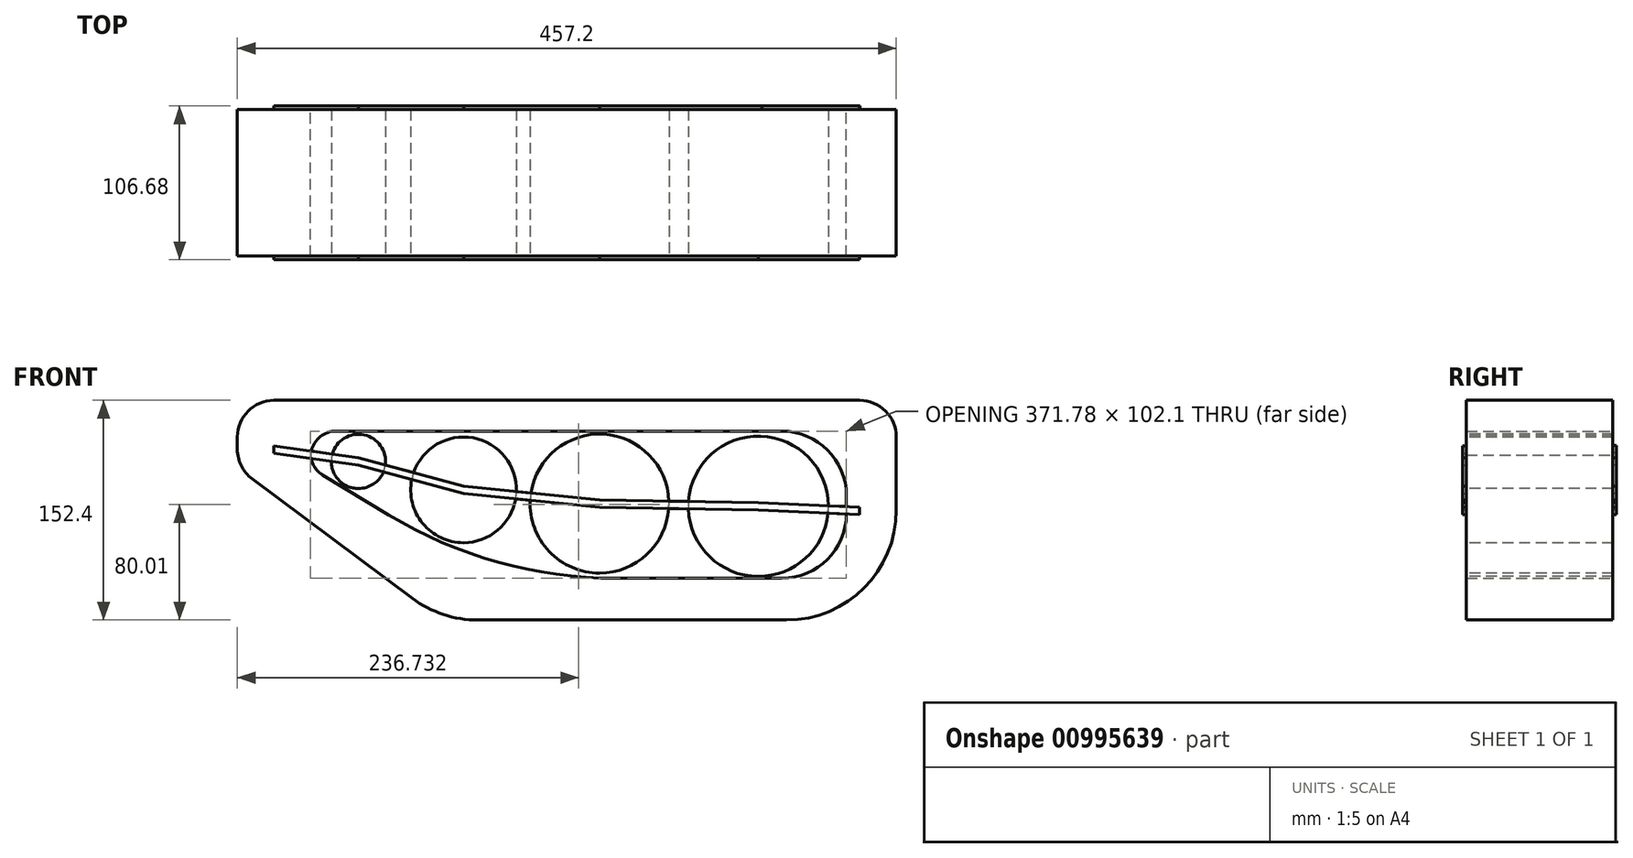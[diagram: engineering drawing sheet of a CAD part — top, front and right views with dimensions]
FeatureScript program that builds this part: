
annotation { "Feature Type Name" : "Feature", "Feature Type Description" : "" }
export const myFeature = defineFeature(function(context is Context, id is Id, definition is map)
    precondition{}
    {
        {
            var Q0;
            Q0=qCreatedBy(makeId("Front.planeOp"),FACE);
            var sketch = newSketch(context, id + "F0", { "sketchPlane" : qUnion([Q0])});
            skLineSegment(sketch, "E0.top", {"start": v(228.6, 76.2) * mm, "end": v(-228.6, 76.2) * mm});
            skLineSegment(sketch, "E0.left", {"start": v(228.6, -76.2) * mm, "end": v(228.6, 76.2) * mm});
            skPoint(sketch, "E0.middle", {"position": v(0, 0) * mm});
            skLineSegment(sketch, "E1", {"start": v(-228.6, 29.46) * mm, "end": v(-86.97, -76.2) * mm});
            skLineSegment(sketch, "E2", {"start": v(-177.8, 29.46) * mm, "end": v(-50.81, -47.24) * mm});
            skLineSegment(sketch, "E3", {"start": v(-50.81, -47.24) * mm, "end": v(194.02, -47.24) * mm});
            skLineSegment(sketch, "E4", {"start": v(-86.97, -76.2) * mm, "end": v(228.6, -76.2) * mm});
            skLineSegment(sketch, "E5", {"start": v(-228.6, 76.2) * mm, "end": v(-228.6, 29.46) * mm});
            skLineSegment(sketch, "E6", {"start": v(-177.8, 29.46) * mm, "end": v(-177.8, 54.86) * mm});
            skLineSegment(sketch, "E7", {"start": v(-177.8, 54.86) * mm, "end": v(194.02, 54.86) * mm});
            skLineSegment(sketch, "E8", {"start": v(194.02, 54.86) * mm, "end": v(194.02, -47.24) * mm});
            skSolve(sketch);
        }
        {
            var Q0;
            Q0=makeQuery(id+"F0.imprint","IMPRINT",FACE,{"disambiguationData":[TD([[makeQuery(id+"F0.imprint","IMPRINT",EDGE,{"derivedFrom":sQuery(id+"F0.wireOp",EDGE,"E0.top")}),1.0]])]});
            extrude(context, id + "F1", {"entities" : qUnion([Q0]), "depth" : 101.6 * mm, "offsetDistance" : 25.4 * mm});
        }
        {
            var Q0;
            Q0=makeQuery(id+"F1.opExtrude","SWEPT_EDGE",EDGE,{"disambiguationData":[OSD([sQuery(id+"F0.wireOp",EDGE,"E0.top"),sQuery(id+"F0.wireOp",EDGE,"E5")])]});
            var Q1;
            Q1=makeQuery(id+"F1.opExtrude","SWEPT_EDGE",EDGE,{"disambiguationData":[OSD([sQuery(id+"F0.wireOp",EDGE,"E1"),sQuery(id+"F0.wireOp",EDGE,"E5")])]});
            fillet(context, id + "F2", {"entities" : qUnion([Q0, Q1]), "radius" : 25.4 * mm, "tangentPropagation" : true, "allowEdgeOverflow" : false});
        }
        {
            var Q0;
            Q0=makeQuery(id+"F1.opExtrude","SWEPT_EDGE",EDGE,{"disambiguationData":[OSD([sQuery(id+"F0.wireOp",EDGE,"E1"),sQuery(id+"F0.wireOp",EDGE,"E4")])]});
            var Q1;
            Q1=makeQuery(id+"F1.opExtrude","SWEPT_EDGE",EDGE,{"disambiguationData":[OSD([sQuery(id+"F0.wireOp",EDGE,"E0.left"),sQuery(id+"F0.wireOp",EDGE,"E4")])]});
            fillet(context, id + "F3", {"entities" : qUnion([Q0, Q1]), "radius" : 76.2 * mm, "tangentPropagation" : true, "allowEdgeOverflow" : false});
        }
        {
            var Q0;
            Q0=makeQuery(id+"F1.opExtrude","SWEPT_EDGE",EDGE,{"disambiguationData":[OSD([sQuery(id+"F0.wireOp",EDGE,"E0.top"),sQuery(id+"F0.wireOp",EDGE,"E0.left")])]});
            fillet(context, id + "F4", {"entities" : qUnion([Q0]), "radius" : 25.4 * mm, "tangentPropagation" : true, "allowEdgeOverflow" : false});
        }
        {
            var Q0;
            Q0=makeQuery(id+"F1.opExtrude","SWEPT_EDGE",EDGE,{"disambiguationData":[OSD([sQuery(id+"F0.wireOp",EDGE,"E2"),sQuery(id+"F0.wireOp",EDGE,"E6")])]});
            var Q1;
            Q1=makeQuery(id+"F1.opExtrude","SWEPT_EDGE",EDGE,{"disambiguationData":[OSD([sQuery(id+"F0.wireOp",EDGE,"E6"),sQuery(id+"F0.wireOp",EDGE,"E7")])]});
            fillet(context, id + "F5", {"entities" : qUnion([Q0, Q1]), "radius" : 17.78 * mm, "tangentPropagation" : true, "allowEdgeOverflow" : false});
        }
        {
            var Q0;
            Q0=makeQuery(id+"F1.opExtrude","SWEPT_EDGE",EDGE,{"disambiguationData":[OSD([sQuery(id+"F0.wireOp",EDGE,"E3"),sQuery(id+"F0.wireOp",EDGE,"E8")])]});
            var Q1;
            Q1=makeQuery(id+"F1.opExtrude","SWEPT_EDGE",EDGE,{"disambiguationData":[OSD([sQuery(id+"F0.wireOp",EDGE,"E7"),sQuery(id+"F0.wireOp",EDGE,"E8")])]});
            fillet(context, id + "F6", {"entities" : qUnion([Q0, Q1]), "radius" : 44.76 * mm, "tangentPropagation" : true, "allowEdgeOverflow" : false});
        }
        {
            var Q0;
            Q0=makeQuery(id+"F1.opExtrude","SWEPT_EDGE",EDGE,{"disambiguationData":[OSD([sQuery(id+"F0.wireOp",EDGE,"E2"),sQuery(id+"F0.wireOp",EDGE,"E3")])]});
            fillet(context, id + "F7", {"entities" : qUnion([Q0]), "radius" : 304.8 * mm, "tangentPropagation" : true, "allowEdgeOverflow" : false});
        }
        {
            var Q0;
            Q0=makeQuery(id+"F1.opExtrude","CAP_FACE",FACE,{"disambiguationData":[OSD([sQuery(id+"F0.wireOp",EDGE,"E0.top"),sQuery(id+"F0.wireOp",EDGE,"E0.left"),sQuery(id+"F0.wireOp",EDGE,"E1"),sQuery(id+"F0.wireOp",EDGE,"E2"),sQuery(id+"F0.wireOp",EDGE,"E3"),sQuery(id+"F0.wireOp",EDGE,"E4"),sQuery(id+"F0.wireOp",EDGE,"E5"),sQuery(id+"F0.wireOp",EDGE,"E6"),sQuery(id+"F0.wireOp",EDGE,"E7"),sQuery(id+"F0.wireOp",EDGE,"E8")])],"isStart":false});
            var sketch = newSketch(context, id + "F8", { "sketchPlane" : qUnion([Q0])});
            skCircle(sketch, "E9", {"center": v(-144.6, 33.85) * mm, "radius": 18.83 * mm});
            skPoint(sketch, "E9.first.point", {"position": v(-138.02, 51.5) * mm});
            skPoint(sketch, "E9.second.point", {"position": v(-146.35, 15.1) * mm});
            skPoint(sketch, "E9.second.point.positionSnap0", {"position": v(-146.35, 10.46) * mm});
            skPoint(sketch, "E9.third.point", {"position": v(-127.18, 26.71) * mm});
            skCircle(sketch, "E10", {"center": v(-71.64, 14.1) * mm, "radius": 36.66 * mm});
            skPoint(sketch, "E10.first.point", {"position": v(-73.36, 50.72) * mm});
            skPoint(sketch, "E10.second.point", {"position": v(-65.62, -22.07) * mm});
            skPoint(sketch, "E10.third.point", {"position": v(-50.52, -15.87) * mm});
            skCircle(sketch, "E11", {"center": v(22.69, 4.6) * mm, "radius": 48.18 * mm});
            skPoint(sketch, "E11.first.point", {"position": v(6.39, 49.94) * mm});
            skPoint(sketch, "E11.second.point", {"position": v(41.23, -39.88) * mm});
            skPoint(sketch, "E11.third.point", {"position": v(61.75, -23.62) * mm});
            skCircle(sketch, "E12", {"center": v(132.93, 2.7) * mm, "radius": 48.63 * mm});
            skPoint(sketch, "E12.first.point", {"position": v(129.96, 51.24) * mm});
            skPoint(sketch, "E12.second.point", {"position": v(126.16, -45.46) * mm});
            skPoint(sketch, "E12.third.point", {"position": v(181.18, -3.34) * mm});
            skLineSegment(sketch, "E13", {"start": v(-203.2, 42.2) * mm, "end": v(-203.2, 44.74) * mm});
            skLineSegment(sketch, "E14", {"start": v(-203.2, 42.2) * mm, "end": v(-203.2, 39.66) * mm});
            skLineSegment(sketch, "E15", {"start": v(203.2, -0.41) * mm, "end": v(203.2, -2.95) * mm});
            skLineSegment(sketch, "E16", {"start": v(203.2, -0.41) * mm, "end": v(203.2, 2.13) * mm});
            skLineSegment(sketch, "E17", {"start": v(-203.2, 44.74) * mm, "end": v(-144.6, 36.39) * mm});
            skLineSegment(sketch, "E18", {"start": v(-144.6, 36.39) * mm, "end": v(-71.64, 16.64) * mm});
            skLineSegment(sketch, "E19", {"start": v(-71.64, 16.64) * mm, "end": v(22.69, 7.14) * mm});
            skLineSegment(sketch, "E20", {"start": v(22.69, 7.14) * mm, "end": v(132.93, 5.24) * mm});
            skLineSegment(sketch, "E21", {"start": v(132.93, 5.24) * mm, "end": v(203.2, 2.13) * mm});
            skLineSegment(sketch, "E22", {"start": v(203.2, -2.95) * mm, "end": v(132.93, 0.16) * mm});
            skLineSegment(sketch, "E23", {"start": v(132.93, 0.16) * mm, "end": v(22.69, 2.06) * mm});
            skLineSegment(sketch, "E24", {"start": v(22.69, 2.06) * mm, "end": v(-71.64, 11.56) * mm});
            skLineSegment(sketch, "E25", {"start": v(-71.64, 11.56) * mm, "end": v(-144.6, 31.3) * mm});
            skLineSegment(sketch, "E26", {"start": v(-144.6, 31.3) * mm, "end": v(-203.2, 39.66) * mm});
            skSolve(sketch);
        }
        {
            var Q0;
            Q0=makeQuery(id+"F8.imprint","IMPRINT",FACE,{"disambiguationData":[TD([[makeQuery(id+"F8.imprint","IMPRINT",EDGE,{"derivedFrom":sQuery(id+"F8.wireOp",EDGE,"E12")}),1.0]])]});
            var Q1;
            Q1=makeQuery(id+"F8.imprint","IMPRINT",FACE,{"disambiguationData":[TD([[makeQuery(id+"F8.imprint","IMPRINT",EDGE,{"derivedFrom":sQuery(id+"F8.wireOp",EDGE,"E11")}),1.0]])]});
            var Q2;
            Q2=makeQuery(id+"F8.imprint","IMPRINT",FACE,{"disambiguationData":[TD([[makeQuery(id+"F8.imprint","IMPRINT",EDGE,{"derivedFrom":sQuery(id+"F8.wireOp",EDGE,"E10")}),1.0]])]});
            var Q3;
            Q3=makeQuery(id+"F8.imprint","IMPRINT",FACE,{"disambiguationData":[TD([[makeQuery(id+"F8.imprint","IMPRINT",EDGE,{"derivedFrom":sQuery(id+"F8.wireOp",EDGE,"E9")}),1.0]])]});
            var Q4;
            {var subQ0=sQuery(id+"F8.wireOp",EDGE,"AqAeLmdH-5IiC-45pe-Ufpz-pEmairjJmkVr");var subQ1=sQuery(id+"F8.wireOp",EDGE,"E12");var subQ2=makeQuery(id+"F8.imprint","INTERSECT",VERTEX,{"disambiguationData":[OD(0.0)],"derivedFrom":[subQ1,subQ0]});Q4=makeQuery(id+"F8.imprint","IMPRINT",FACE,{"disambiguationData":[TD([[makeQuery(id+"F8.imprint","IMPRINT",EDGE,{"disambiguationData":[TD([[subQ2,-1.0]])],"derivedFrom":subQ1}),1.0]])]});}
            var Q5;
            {var subQ0=sQuery(id+"F8.wireOp",EDGE,"RcY1my2E-DYNY-53v3-rrAe-4BZeLiWxirUP");var subQ1=sQuery(id+"F8.wireOp",EDGE,"E12");var subQ2=makeQuery(id+"F8.imprint","INTERSECT",VERTEX,{"disambiguationData":[OD(0.0)],"derivedFrom":[subQ1,subQ0]});Q5=makeQuery(id+"F8.imprint","IMPRINT",FACE,{"disambiguationData":[TD([[makeQuery(id+"F8.imprint","IMPRINT",EDGE,{"disambiguationData":[TD([[subQ2,1.0]])],"derivedFrom":subQ1}),1.0]])]});}
            var Q6;
            {var subQ0=sQuery(id+"F8.wireOp",EDGE,"AqAeLmdH-5IiC-45pe-Ufpz-pEmairjJmkVr");var subQ1=sQuery(id+"F8.wireOp",EDGE,"E11");var subQ2=makeQuery(id+"F8.imprint","INTERSECT",VERTEX,{"disambiguationData":[OD(0.0)],"derivedFrom":[subQ1,subQ0]});Q6=makeQuery(id+"F8.imprint","IMPRINT",FACE,{"disambiguationData":[TD([[makeQuery(id+"F8.imprint","IMPRINT",EDGE,{"disambiguationData":[TD([[subQ2,1.0]])],"derivedFrom":subQ1}),1.0]])]});}
            var Q7;
            {var subQ0=sQuery(id+"F8.wireOp",EDGE,"RcY1my2E-DYNY-53v3-rrAe-4BZeLiWxirUP");var subQ1=sQuery(id+"F8.wireOp",EDGE,"E11");var subQ2=makeQuery(id+"F8.imprint","INTERSECT",VERTEX,{"disambiguationData":[OD(0.0)],"derivedFrom":[subQ1,subQ0]});Q7=makeQuery(id+"F8.imprint","IMPRINT",FACE,{"disambiguationData":[TD([[makeQuery(id+"F8.imprint","IMPRINT",EDGE,{"disambiguationData":[TD([[subQ2,-1.0]])],"derivedFrom":subQ1}),1.0]])]});}
            var Q8;
            {var subQ0=sQuery(id+"F8.wireOp",EDGE,"AqAeLmdH-5IiC-45pe-Ufpz-pEmairjJmkVr");var subQ1=sQuery(id+"F8.wireOp",EDGE,"E10");var subQ2=makeQuery(id+"F8.imprint","INTERSECT",VERTEX,{"disambiguationData":[OD(0.0)],"derivedFrom":[subQ1,subQ0]});Q8=makeQuery(id+"F8.imprint","IMPRINT",FACE,{"disambiguationData":[TD([[makeQuery(id+"F8.imprint","IMPRINT",EDGE,{"disambiguationData":[TD([[subQ2,1.0]])],"derivedFrom":subQ1}),1.0]])]});}
            var Q9;
            {var subQ0=sQuery(id+"F8.wireOp",EDGE,"RcY1my2E-DYNY-53v3-rrAe-4BZeLiWxirUP");var subQ1=sQuery(id+"F8.wireOp",EDGE,"E10");var subQ2=makeQuery(id+"F8.imprint","INTERSECT",VERTEX,{"disambiguationData":[OD(0.0)],"derivedFrom":[subQ1,subQ0]});Q9=makeQuery(id+"F8.imprint","IMPRINT",FACE,{"disambiguationData":[TD([[makeQuery(id+"F8.imprint","IMPRINT",EDGE,{"disambiguationData":[TD([[subQ2,-1.0]])],"derivedFrom":subQ1}),1.0]])]});}
            var Q10;
            {var subQ0=sQuery(id+"F8.wireOp",EDGE,"AqAeLmdH-5IiC-45pe-Ufpz-pEmairjJmkVr");var subQ1=sQuery(id+"F8.wireOp",EDGE,"E9");var subQ2=makeQuery(id+"F8.imprint","INTERSECT",VERTEX,{"disambiguationData":[OD(0.0)],"derivedFrom":[subQ1,subQ0]});Q10=makeQuery(id+"F8.imprint","IMPRINT",FACE,{"disambiguationData":[TD([[makeQuery(id+"F8.imprint","IMPRINT",EDGE,{"disambiguationData":[TD([[subQ2,-1.0]])],"derivedFrom":subQ1}),1.0]])]});}
            var Q11;
            {var subQ0=sQuery(id+"F8.wireOp",EDGE,"RcY1my2E-DYNY-53v3-rrAe-4BZeLiWxirUP");var subQ1=sQuery(id+"F8.wireOp",EDGE,"E9");var subQ2=makeQuery(id+"F8.imprint","INTERSECT",VERTEX,{"disambiguationData":[OD(0.0)],"derivedFrom":[subQ1,subQ0]});Q11=makeQuery(id+"F8.imprint","IMPRINT",FACE,{"disambiguationData":[TD([[makeQuery(id+"F8.imprint","IMPRINT",EDGE,{"disambiguationData":[TD([[subQ2,1.0]])],"derivedFrom":subQ1}),1.0]])]});}
            var Q12;
            {var subQ0=sQuery(id+"F8.wireOp",EDGE,"E17");var subQ1=sQuery(id+"F8.wireOp",EDGE,"E9");var subQ2=makeQuery(id+"F8.imprint","INTERSECT",VERTEX,{"derivedFrom":[subQ1,subQ0]});Q12=makeQuery(id+"F8.imprint","IMPRINT",FACE,{"disambiguationData":[TD([[makeQuery(id+"F8.imprint","IMPRINT",EDGE,{"disambiguationData":[TD([[subQ2,1.0]])],"derivedFrom":subQ1}),1.0]])]});}
            var Q13;
            {var subQ0=sQuery(id+"F8.wireOp",EDGE,"E18");var subQ1=sQuery(id+"F8.wireOp",EDGE,"E10");var subQ2=makeQuery(id+"F8.imprint","INTERSECT",VERTEX,{"derivedFrom":[subQ1,subQ0]});Q13=makeQuery(id+"F8.imprint","IMPRINT",FACE,{"disambiguationData":[TD([[makeQuery(id+"F8.imprint","IMPRINT",EDGE,{"disambiguationData":[TD([[subQ2,1.0]])],"derivedFrom":subQ1}),1.0]])]});}
            var Q14;
            {var subQ0=sQuery(id+"F8.wireOp",EDGE,"E19");var subQ1=sQuery(id+"F8.wireOp",EDGE,"E11");var subQ2=makeQuery(id+"F8.imprint","INTERSECT",VERTEX,{"derivedFrom":[subQ1,subQ0]});Q14=makeQuery(id+"F8.imprint","IMPRINT",FACE,{"disambiguationData":[TD([[makeQuery(id+"F8.imprint","IMPRINT",EDGE,{"disambiguationData":[TD([[subQ2,1.0]])],"derivedFrom":subQ1}),1.0]])]});}
            var Q15;
            {var subQ0=sQuery(id+"F8.wireOp",EDGE,"E20");var subQ1=sQuery(id+"F8.wireOp",EDGE,"E12");var subQ2=makeQuery(id+"F8.imprint","INTERSECT",VERTEX,{"derivedFrom":[subQ1,subQ0]});Q15=makeQuery(id+"F8.imprint","IMPRINT",FACE,{"disambiguationData":[TD([[makeQuery(id+"F8.imprint","IMPRINT",EDGE,{"disambiguationData":[TD([[subQ2,1.0]])],"derivedFrom":subQ1}),1.0]])]});}
            var Q16;
            {var subQ0=sQuery(id+"F8.wireOp",EDGE,"E23");var subQ1=sQuery(id+"F8.wireOp",EDGE,"E12");var subQ2=makeQuery(id+"F8.imprint","INTERSECT",VERTEX,{"derivedFrom":[subQ1,subQ0]});Q16=makeQuery(id+"F8.imprint","IMPRINT",FACE,{"disambiguationData":[TD([[makeQuery(id+"F8.imprint","IMPRINT",EDGE,{"disambiguationData":[TD([[subQ2,-1.0]])],"derivedFrom":subQ1}),1.0]])]});}
            var Q17;
            {var subQ0=sQuery(id+"F8.wireOp",EDGE,"E24");var subQ1=sQuery(id+"F8.wireOp",EDGE,"E11");var subQ2=makeQuery(id+"F8.imprint","INTERSECT",VERTEX,{"derivedFrom":[subQ1,subQ0]});Q17=makeQuery(id+"F8.imprint","IMPRINT",FACE,{"disambiguationData":[TD([[makeQuery(id+"F8.imprint","IMPRINT",EDGE,{"disambiguationData":[TD([[subQ2,-1.0]])],"derivedFrom":subQ1}),1.0]])]});}
            var Q18;
            {var subQ0=sQuery(id+"F8.wireOp",EDGE,"E25");var subQ1=sQuery(id+"F8.wireOp",EDGE,"E10");var subQ2=makeQuery(id+"F8.imprint","INTERSECT",VERTEX,{"derivedFrom":[subQ1,subQ0]});Q18=makeQuery(id+"F8.imprint","IMPRINT",FACE,{"disambiguationData":[TD([[makeQuery(id+"F8.imprint","IMPRINT",EDGE,{"disambiguationData":[TD([[subQ2,-1.0]])],"derivedFrom":subQ1}),1.0]])]});}
            var Q19;
            {var subQ0=sQuery(id+"F8.wireOp",EDGE,"E26");var subQ1=sQuery(id+"F8.wireOp",EDGE,"E9");var subQ2=makeQuery(id+"F8.imprint","INTERSECT",VERTEX,{"derivedFrom":[subQ1,subQ0]});Q19=makeQuery(id+"F8.imprint","IMPRINT",FACE,{"disambiguationData":[TD([[makeQuery(id+"F8.imprint","IMPRINT",EDGE,{"disambiguationData":[TD([[subQ2,-1.0]])],"derivedFrom":subQ1}),1.0]])]});}
            extrude(context, id + "F9", {"entities" : qUnion([Q0, Q1, Q2, Q3, Q4, Q5, Q6, Q7, Q8, Q9, Q10, Q11, Q12, Q13, Q14, Q15, Q16, Q17, Q18, Q19]), "depth" : -101.6 * mm, "offsetDistance" : 25.4 * mm});
        }
        {
            var Q0;
            {var subQ1=sQuery(id+"F8.wireOp",EDGE,"E19");var subQ3=sQuery(id+"F8.wireOp",EDGE,"E11");var subQ4=makeQuery(id+"F8.imprint","INTERSECT",VERTEX,{"derivedFrom":[subQ3,subQ1]});Q0=makeQuery(id+"F8.imprint","IMPRINT",FACE,{"disambiguationData":[TD([[makeQuery(id+"F8.imprint","IMPRINT",EDGE,{"disambiguationData":[TD([[subQ4,-1.0]])],"derivedFrom":subQ3}),1.0]])]});}
            var Q1;
            {var subQ0=sQuery(id+"F8.wireOp",EDGE,"E24");var subQ1=sQuery(id+"F8.wireOp",EDGE,"E10");var subQ2=makeQuery(id+"F8.imprint","INTERSECT",VERTEX,{"derivedFrom":[subQ1,subQ0]});Q1=makeQuery(id+"F8.imprint","IMPRINT",FACE,{"disambiguationData":[TD([[makeQuery(id+"F8.imprint","IMPRINT",EDGE,{"disambiguationData":[TD([[subQ2,-1.0]])],"derivedFrom":subQ1}),-1.0]])]});}
            var Q2;
            {var subQ3=sQuery(id+"F8.wireOp",EDGE,"E10");var subQ6=sQuery(id+"F8.wireOp",EDGE,"E25");var subQ7=makeQuery(id+"F8.imprint","INTERSECT",VERTEX,{"derivedFrom":[subQ3,subQ6]});Q2=makeQuery(id+"F8.imprint","IMPRINT",FACE,{"disambiguationData":[TD([[makeQuery(id+"F8.imprint","IMPRINT",EDGE,{"disambiguationData":[TD([[subQ7,1.0]])],"derivedFrom":subQ3}),1.0]])]});}
            var Q3;
            {var subQ0=sQuery(id+"F8.wireOp",EDGE,"E20");var subQ1=sQuery(id+"F8.wireOp",EDGE,"E11");var subQ2=makeQuery(id+"F8.imprint","INTERSECT",VERTEX,{"derivedFrom":[subQ1,subQ0]});Q3=makeQuery(id+"F8.imprint","IMPRINT",FACE,{"disambiguationData":[TD([[makeQuery(id+"F8.imprint","IMPRINT",EDGE,{"disambiguationData":[TD([[subQ2,1.0]])],"derivedFrom":subQ1}),-1.0]])]});}
            var Q4;
            {var subQ1=sQuery(id+"F8.wireOp",EDGE,"E20");var subQ3=sQuery(id+"F8.wireOp",EDGE,"E12");var subQ5=makeQuery(id+"F8.imprint","INTERSECT",VERTEX,{"derivedFrom":[subQ3,subQ1]});Q4=makeQuery(id+"F8.imprint","IMPRINT",FACE,{"disambiguationData":[TD([[makeQuery(id+"F8.imprint","IMPRINT",EDGE,{"disambiguationData":[TD([[subQ5,-1.0]])],"derivedFrom":subQ3}),1.0]])]});}
            var Q5;
            {var subQ1=sQuery(id+"F8.wireOp",EDGE,"E12");var subQ7=sQuery(id+"F8.wireOp",EDGE,"E21");var subQ8=makeQuery(id+"F8.imprint","INTERSECT",VERTEX,{"derivedFrom":[subQ1,subQ7]});Q5=makeQuery(id+"F8.imprint","IMPRINT",FACE,{"disambiguationData":[TD([[makeQuery(id+"F8.imprint","IMPRINT",EDGE,{"disambiguationData":[TD([[subQ8,1.0]])],"derivedFrom":subQ1}),-1.0]])]});}
            var Q6;
            {var subQ3=sQuery(id+"F8.wireOp",EDGE,"E9");var subQ6=sQuery(id+"F8.wireOp",EDGE,"E26");var subQ7=makeQuery(id+"F8.imprint","INTERSECT",VERTEX,{"derivedFrom":[subQ3,subQ6]});Q6=makeQuery(id+"F8.imprint","IMPRINT",FACE,{"disambiguationData":[TD([[makeQuery(id+"F8.imprint","IMPRINT",EDGE,{"disambiguationData":[TD([[subQ7,1.0]])],"derivedFrom":subQ3}),1.0]])]});}
            var Q7;
            {var subQ0=sQuery(id+"F8.wireOp",EDGE,"E25");var subQ1=sQuery(id+"F8.wireOp",EDGE,"E9");var subQ2=makeQuery(id+"F8.imprint","INTERSECT",VERTEX,{"derivedFrom":[subQ1,subQ0]});Q7=makeQuery(id+"F8.imprint","IMPRINT",FACE,{"disambiguationData":[TD([[makeQuery(id+"F8.imprint","IMPRINT",EDGE,{"disambiguationData":[TD([[subQ2,-1.0]])],"derivedFrom":subQ1}),-1.0]])]});}
            var Q8;
            {var subQ0=sQuery(id+"F8.wireOp",EDGE,"E26");var subQ1=sQuery(id+"F8.wireOp",EDGE,"E9");var subQ2=makeQuery(id+"F8.imprint","INTERSECT",VERTEX,{"derivedFrom":[subQ1,subQ0]});Q8=makeQuery(id+"F8.imprint","IMPRINT",FACE,{"disambiguationData":[TD([[makeQuery(id+"F8.imprint","IMPRINT",EDGE,{"disambiguationData":[TD([[subQ2,1.0]])],"derivedFrom":subQ1}),-1.0]])]});}
            var Q9;
            {var subQ8=sQuery(id+"F8.wireOp",EDGE,"E13");Q9=makeQuery(id+"F8.imprint","IMPRINT",FACE,{"disambiguationData":[TD([[makeQuery(id+"F8.imprint","IMPRINT",EDGE,{"derivedFrom":subQ8}),-1.0]])]});}
            var Q10;
            {var subQ1=sQuery(id+"F8.wireOp",EDGE,"E15");Q10=makeQuery(id+"F8.imprint","IMPRINT",FACE,{"disambiguationData":[TD([[makeQuery(id+"F8.imprint","IMPRINT",EDGE,{"derivedFrom":subQ1}),-1.0]])]});}
            extrude(context, id + "F10", {"entities" : qUnion([Q0, Q1, Q2, Q3, Q4, Q5, Q6, Q7, Q8, Q9, Q10]), "depth" : 2.54 * mm, "offsetDistance" : 25.4 * mm});
        }
        {
            var Q0;
            Q0=makeQuery(id+"F1.opExtrude","CAP_FACE",FACE,{"disambiguationData":[OSD([sQuery(id+"F0.wireOp",EDGE,"E0.top"),sQuery(id+"F0.wireOp",EDGE,"E0.left"),sQuery(id+"F0.wireOp",EDGE,"E1"),sQuery(id+"F0.wireOp",EDGE,"E2"),sQuery(id+"F0.wireOp",EDGE,"E3"),sQuery(id+"F0.wireOp",EDGE,"E4"),sQuery(id+"F0.wireOp",EDGE,"E5"),sQuery(id+"F0.wireOp",EDGE,"E6"),sQuery(id+"F0.wireOp",EDGE,"E7"),sQuery(id+"F0.wireOp",EDGE,"E8")])],"isStart":true});
            var sketch = newSketch(context, id + "F11", { "sketchPlane" : qUnion([Q0])});
            skPoint(sketch, "E27", {"position": v(203.2, 39.82) * mm});
            skPoint(sketch, "E28", {"position": v(203.2, 44.78) * mm});
            skPoint(sketch, "E29", {"position": v(144.73, 31.4) * mm});
            skPoint(sketch, "E30", {"position": v(144.68, 36.45) * mm});
            skPoint(sketch, "E31", {"position": v(71.6, 16.64) * mm});
            skPoint(sketch, "E32", {"position": v(71.48, 11.57) * mm});
            skPoint(sketch, "E33", {"position": v(-22.78, 7.14) * mm});
            skPoint(sketch, "E34", {"position": v(-22.57, 2.01) * mm});
            skPoint(sketch, "E35", {"position": v(-135.4, 5.23) * mm});
            skPoint(sketch, "E36", {"position": v(-134.57, 0) * mm});
            skPoint(sketch, "E37", {"position": v(-203.18, 2.12) * mm});
            skPoint(sketch, "E38", {"position": v(-203.27, -2.98) * mm});
            skLineSegment(sketch, "E39", {"start": v(-203.18, 2.12) * mm, "end": v(-203.27, -2.98) * mm});
            skLineSegment(sketch, "E40", {"start": v(-203.18, 2.12) * mm, "end": v(-135.4, 5.23) * mm});
            skLineSegment(sketch, "E41", {"start": v(-135.4, 5.23) * mm, "end": v(-22.78, 7.14) * mm});
            skLineSegment(sketch, "E42", {"start": v(-22.78, 7.14) * mm, "end": v(71.6, 16.64) * mm});
            skLineSegment(sketch, "E43", {"start": v(203.2, 44.78) * mm, "end": v(144.68, 36.45) * mm});
            skLineSegment(sketch, "E44", {"start": v(144.68, 36.45) * mm, "end": v(71.6, 16.64) * mm});
            skLineSegment(sketch, "E45", {"start": v(203.2, 44.78) * mm, "end": v(203.2, 39.82) * mm});
            skLineSegment(sketch, "E46", {"start": v(203.2, 39.82) * mm, "end": v(144.73, 31.4) * mm});
            skLineSegment(sketch, "E47", {"start": v(144.73, 31.4) * mm, "end": v(71.48, 11.57) * mm});
            skLineSegment(sketch, "E48", {"start": v(71.48, 11.57) * mm, "end": v(-22.57, 2.01) * mm});
            skLineSegment(sketch, "E49", {"start": v(-22.57, 2.01) * mm, "end": v(-134.57, 0) * mm});
            skLineSegment(sketch, "E50", {"start": v(-203.27, -2.98) * mm, "end": v(-134.57, 0) * mm});
            skSolve(sketch);
        }
        {
            var Q0;
            {var subQ21=sQuery(id+"F11.wireOp",EDGE,"E41");Q0=makeQuery(id+"F11.imprint","IMPRINT",FACE,{"disambiguationData":[TD([[makeQuery(id+"F11.imprint","IMPRINT",EDGE,{"derivedFrom":subQ21}),-1.0]])]});}
            var Q1;
            {var subQ9=sQuery(id+"F11.wireOp",EDGE,"E45");Q1=makeQuery(id+"F11.imprint","IMPRINT",FACE,{"disambiguationData":[TD([[makeQuery(id+"F11.imprint","IMPRINT",EDGE,{"derivedFrom":subQ9}),-1.0]])]});}
            var Q2;
            {var subQ1=sQuery(id+"F11.wireOp",EDGE,"E39");Q2=makeQuery(id+"F11.imprint","IMPRINT",FACE,{"disambiguationData":[TD([[makeQuery(id+"F11.imprint","IMPRINT",EDGE,{"derivedFrom":subQ1}),1.0]])]});}
            extrude(context, id + "F12", {"entities" : qUnion([Q0, Q1, Q2]), "depth" : 2.54 * mm, "offsetDistance" : 25.4 * mm});
        }
    });
